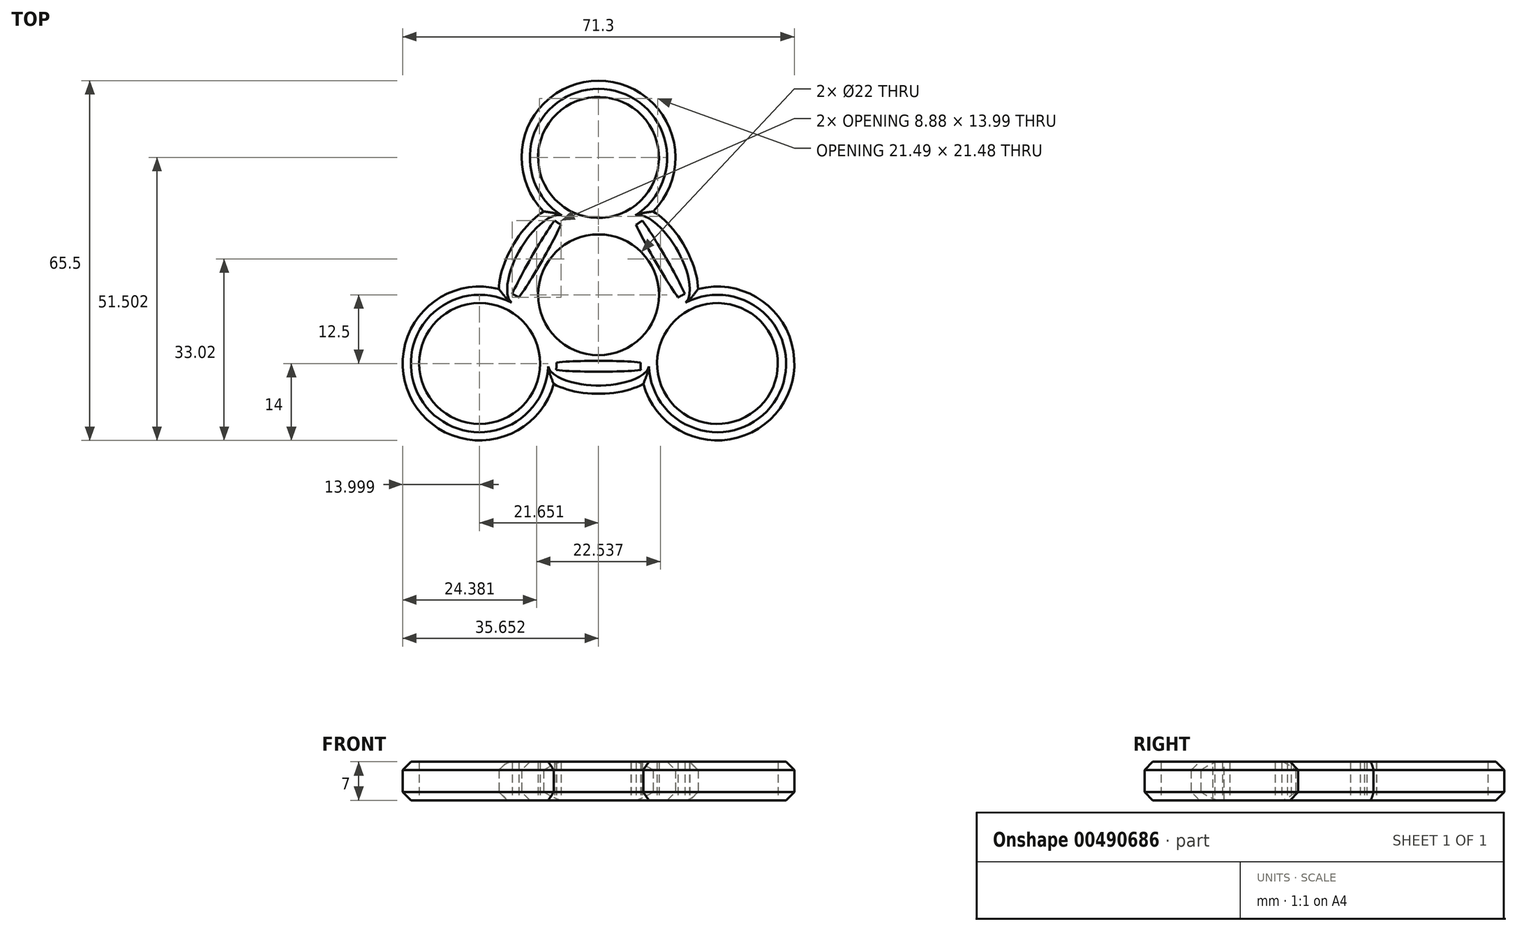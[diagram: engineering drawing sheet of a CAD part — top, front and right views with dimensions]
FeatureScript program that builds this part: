
annotation { "Feature Type Name" : "Feature", "Feature Type Description" : "" }
export const myFeature = defineFeature(function(context is Context, id is Id, definition is map)
    precondition{}
    {
        {
            var Q0;
            Q0=qCreatedBy(makeId("Top.planeOp"),FACE);
            var sketch = newSketch(context, id + "F0", { "sketchPlane" : qUnion([Q0])});
            skCircle(sketch, "E0", {"center": v(0, 0) * mm, "radius": 11 * mm});
            skCircle(sketch, "E1", {"center": v(0, 25) * mm, "radius": 11 * mm});
            skCircle(sketch, "E2.0", {"center": v(0, 25) * mm, "radius": 14 * mm});
            skCircle(sketch, "E3.1.0", {"center": v(-21.65, -12.5) * mm, "radius": 14 * mm});
            skCircle(sketch, "E3.1.1", {"center": v(-21.65, -12.5) * mm, "radius": 11 * mm});
            skCircle(sketch, "E3.2.0", {"center": v(21.65, -12.5) * mm, "radius": 14 * mm});
            skCircle(sketch, "E3.2.1", {"center": v(21.65, -12.5) * mm, "radius": 11 * mm});
            skLineSegment(sketch, "E4", {"start": v(0, 0) * mm, "end": v(9.53, 5.5) * mm});
            skLineSegment(sketch, "E5", {"start": v(9.53, 5.5) * mm, "end": v(11.26, 6.5) * mm});
            skLineSegment(sketch, "E6", {"start": v(5.9, 15.72) * mm, "end": v(0, 25) * mm});
            skLineSegment(sketch, "E7", {"start": v(11.26, 6.5) * mm, "end": v(15.59, 9) * mm});
            skEllipticalArc(sketch, "E8.trimOffspring", {});
            skEllipticalArc(sketch, "E9.trimOffspring", {});
            skPoint(sketch, "E10", {"position": v(10.4, 6) * mm});
            skEllipticalArc(sketch, "E11", {});
            skEllipticalArc(sketch, "E12.trimOffspring", {});
            skEllipticalArc(sketch, "E13.trimOffspring", {});
            skEllipticalArc(sketch, "E14.trimOffspring", {});
            skEllipticalArc(sketch, "E15.trimOffspring", {});
            skEllipticalArc(sketch, "E16.trimOffspring", {});
            skEllipticalArc(sketch, "E17.1.0", {});
            skEllipticalArc(sketch, "E17.1.1", {});
            skEllipticalArc(sketch, "E17.1.2", {});
            skEllipticalArc(sketch, "E17.2.0", {});
            skEllipticalArc(sketch, "E17.2.1", {});
            skEllipticalArc(sketch, "E17.2.2", {});
            const initialGuessF0  = {"E8.trimOffspring": [0.01125833024919717, 0.0065, 0.8660254037844385, 0.5, 0.005, 0.010660936978134876, 4.682803479661057, 4.717966405982033], "E9.trimOffspring": [0.01125833024919717, 0.0065, -0.8660254037844385, -0.5, 0.002, 0.010661807649901498, 1.556852383236011, 1.584740270353764], "E11": [0.01125833024919717, 0.0065, -0.8660254037844386, -0.5, 0.001, 0.010664918934220318, 4.684498381173167, 4.740279579596198], "E8.trimOffspring": [0.01125833024919717, 0.0065, 0.8660254037844385, 0.5, 0.005, 0.01066093697813487, 4.682803479661057, 4.7179664059820325], "E12.trimOffspring": [0.01125833024919717, 0.0065, 0.8660254037844385, 0.5, 0.005, 0.01066093697813487, 1.565218901197495, 1.6003818275303778], "E13.trimOffspring": [0.01125833024919717, 0.0065, -0.8660254037844386, -0.5, 0.001, 0.010664918934220318, 5.482987378517246, 0.8001979286625209], "E14.trimOffspring": [0.01125833024919717, 0.0065, 0.8660254037844385, 0.5, 0.005, 0.01066093697813487, 5.412354235743484, 0.8708310714359309], "E15.trimOffspring": [0.01125833024919717, 0.0065, -0.8660254037844386, -0.5, 0.001, 0.010664918934220318, 2.3347169685646114, 3.9484683386147137], "E16.trimOffspring": [0.01125833024919717, 0.0065, -0.8660254037844386, -0.5, 0.001, 0.010664918934220318, 1.5429057275836113, 1.5986869260061582], "E17.1.0": [-0.011258330249198182, 0.0065, -0.8660254037844388, 0.5, 0.005, 0.01066093697813487, 5.412354235743484, 0.8708310714359309], "E17.1.1": [-0.01125833024919818, 0.0065, 0.8660254037844388, -0.5, 0.001, 0.010664918934220318, 2.3347169685646114, 3.9484683386147137], "E17.1.2": [-0.01125833024919818, 0.0065, 0.8660254037844388, -0.5, 0.001, 0.010664918934220318, 5.482987378517246, 0.8001979286625209], "E17.2.0": [0, -0.013, 0, -1, 0.005, 0.01066093697813487, 5.412354235743484, 0.8708310714359309], "E17.2.1": [0, -0.013, 0, 1, 0.001, 0.010664918934220318, 2.3347169685646114, 3.9484683386147137], "E17.2.2": [0, -0.013, 0, 1, 0.001, 0.010664918934220318, 5.482987378517246, 0.8001979286625209]};
            skSetInitialGuess(sketch, initialGuessF0);
            skSolve(sketch);
        }
        {
            var Q0;
            {var subQ0=sQuery(id+"F0.wireOp",EDGE,"E12.trimOffspring");var subQ3=sQuery(id+"F0.wireOp",EDGE,"E1");var subQ13=makeQuery(id+"F0.imprint","INTERSECT",VERTEX,{"derivedFrom":[subQ3,subQ0]});Q0=makeQuery(id+"F0.imprint","IMPRINT",FACE,{"disambiguationData":[TD([[makeQuery(id+"F0.imprint","IMPRINT",EDGE,{"disambiguationData":[TD([[subQ13,1.0]])],"derivedFrom":subQ3}),-1.0]])]});}
            var Q1;
            {var subQ0=sQuery(id+"F0.wireOp",EDGE,"E14.trimOffspring");var subQ1=sQuery(id+"F0.wireOp",EDGE,"E2.0");var subQ2=makeQuery(id+"F0.imprint","INTERSECT",VERTEX,{"derivedFrom":[subQ1,subQ0]});Q1=makeQuery(id+"F0.imprint","IMPRINT",FACE,{"disambiguationData":[TD([[makeQuery(id+"F0.imprint","IMPRINT",EDGE,{"disambiguationData":[TD([[subQ2,1.0]])],"derivedFrom":subQ1}),-1.0]])]});}
            var Q2;
            {var subQ0=sQuery(id+"F0.wireOp",EDGE,"E14.trimOffspring");var subQ1=sQuery(id+"F0.wireOp",EDGE,"E3.2.0");var subQ2=makeQuery(id+"F0.imprint","INTERSECT",VERTEX,{"derivedFrom":[subQ1,subQ0]});Q2=makeQuery(id+"F0.imprint","IMPRINT",FACE,{"disambiguationData":[TD([[makeQuery(id+"F0.imprint","IMPRINT",EDGE,{"disambiguationData":[TD([[subQ2,-1.0]])],"derivedFrom":subQ1}),-1.0]])]});}
            var Q3;
            {var subQ0=sQuery(id+"F0.wireOp",EDGE,"E5");var subQ1=sQuery(id+"F0.wireOp",EDGE,"E0");var subQ2=makeQuery(id+"F0.imprint","INTERSECT",VERTEX,{"derivedFrom":[subQ1,subQ0]});Q3=makeQuery(id+"F0.imprint","IMPRINT",FACE,{"disambiguationData":[TD([[makeQuery(id+"F0.imprint","IMPRINT",EDGE,{"disambiguationData":[TD([[subQ2,-1.0]])],"derivedFrom":subQ1}),-1.0]])]});}
            var Q4;
            {var subQ0=sQuery(id+"F0.wireOp",EDGE,"E5");var subQ1=sQuery(id+"F0.wireOp",EDGE,"E0");var subQ2=makeQuery(id+"F0.imprint","INTERSECT",VERTEX,{"derivedFrom":[subQ1,subQ0]});Q4=makeQuery(id+"F0.imprint","IMPRINT",FACE,{"disambiguationData":[TD([[makeQuery(id+"F0.imprint","IMPRINT",EDGE,{"disambiguationData":[TD([[subQ2,1.0]])],"derivedFrom":subQ1}),-1.0]])]});}
            var Q5;
            {var subQ5=sQuery(id+"F0.wireOp",EDGE,"E17.1.2");Q5=makeQuery(id+"F0.imprint","IMPRINT",FACE,{"disambiguationData":[TD([[makeQuery(id+"F0.imprint","IMPRINT",EDGE,{"derivedFrom":subQ5}),-1.0]])]});}
            var Q6;
            {var subQ0=sQuery(id+"F0.wireOp",EDGE,"E17.1.0");Q6=makeQuery(id+"F0.imprint","IMPRINT",FACE,{"disambiguationData":[TD([[makeQuery(id+"F0.imprint","IMPRINT",EDGE,{"derivedFrom":subQ0}),1.0]])]});}
            var Q7;
            Q7=makeQuery(id+"F0.imprint","IMPRINT",FACE,{"disambiguationData":[TD([[makeQuery(id+"F0.imprint","IMPRINT",EDGE,{"derivedFrom":sQuery(id+"F0.wireOp",EDGE,"E3.1.1")}),-1.0]])]});
            var Q8;
            {var subQ5=sQuery(id+"F0.wireOp",EDGE,"E17.2.2");Q8=makeQuery(id+"F0.imprint","IMPRINT",FACE,{"disambiguationData":[TD([[makeQuery(id+"F0.imprint","IMPRINT",EDGE,{"derivedFrom":subQ5}),-1.0]])]});}
            var Q9;
            {var subQ0=sQuery(id+"F0.wireOp",EDGE,"E17.2.0");Q9=makeQuery(id+"F0.imprint","IMPRINT",FACE,{"disambiguationData":[TD([[makeQuery(id+"F0.imprint","IMPRINT",EDGE,{"derivedFrom":subQ0}),1.0]])]});}
            var Q10;
            {var subQ7=sQuery(id+"F0.wireOp",EDGE,"E3.2.0");var subQ8=makeQuery(id+"F0.imprint","INTERSECT",VERTEX,{"derivedFrom":[subQ7,sQuery(id+"F0.wireOp",EDGE,"E14.trimOffspring")]});Q10=makeQuery(id+"F0.imprint","IMPRINT",FACE,{"disambiguationData":[TD([[makeQuery(id+"F0.imprint","IMPRINT",EDGE,{"disambiguationData":[TD([[subQ8,-1.0]])],"derivedFrom":subQ7}),1.0]])]});}
            extrude(context, id + "F1", {"entities" : qUnion([Q0, Q1, Q2, Q3, Q4, Q5, Q6, Q7, Q8, Q9, Q10]), "depth" : 7 * mm});
        }
        {
            var Q0;
            {var subQ0=sQuery(id+"F0.wireOp",EDGE,"E2.0");Q0=makeQuery(id+"F1.opExtrude","CAP_EDGE",EDGE,{"disambiguationData":[OSD([subQ0]),TDD([makeQuery(id+"F0.imprint","IMPRINT",EDGE,{"disambiguationData":[TD([[makeQuery(id+"F0.imprint","INTERSECT",VERTEX,{"derivedFrom":[subQ0,sQuery(id+"F0.wireOp",EDGE,"E14.trimOffspring")]}),-1.0]])],"derivedFrom":subQ0})])],"isStart":false});}
            var Q1;
            Q1=makeQuery(id+"F1.opExtrude","CAP_EDGE",EDGE,{"disambiguationData":[OSD([sQuery(id+"F0.wireOp",EDGE,"E17.1.0")])],"isStart":false});
            var Q2;
            {var subQ0=sQuery(id+"F0.wireOp",EDGE,"E3.1.0");Q2=makeQuery(id+"F1.opExtrude","CAP_EDGE",EDGE,{"disambiguationData":[OSD([subQ0]),TDD([makeQuery(id+"F0.imprint","IMPRINT",EDGE,{"disambiguationData":[TD([[makeQuery(id+"F0.imprint","INTERSECT",VERTEX,{"derivedFrom":[subQ0,sQuery(id+"F0.wireOp",EDGE,"E17.1.0")]}),-1.0]])],"derivedFrom":subQ0})])],"isStart":false});}
            var Q3;
            Q3=makeQuery(id+"F1.opExtrude","CAP_EDGE",EDGE,{"disambiguationData":[OSD([sQuery(id+"F0.wireOp",EDGE,"E17.2.0")])],"isStart":false});
            var Q4;
            {var subQ0=sQuery(id+"F0.wireOp",EDGE,"E3.2.0");Q4=makeQuery(id+"F1.opExtrude","CAP_EDGE",EDGE,{"disambiguationData":[OSD([subQ0]),TDD([makeQuery(id+"F0.imprint","IMPRINT",EDGE,{"disambiguationData":[TD([[makeQuery(id+"F0.imprint","INTERSECT",VERTEX,{"derivedFrom":[subQ0,sQuery(id+"F0.wireOp",EDGE,"E14.trimOffspring")]}),1.0]])],"derivedFrom":subQ0})])],"isStart":false});}
            var Q5;
            Q5=makeQuery(id+"F1.opExtrude","CAP_EDGE",EDGE,{"disambiguationData":[OSD([sQuery(id+"F0.wireOp",EDGE,"E14.trimOffspring")])],"isStart":false});
            var Q6;
            {var subQ0=sQuery(id+"F0.wireOp",EDGE,"E3.2.0");Q6=makeQuery(id+"F1.opExtrude","CAP_EDGE",EDGE,{"disambiguationData":[OSD([subQ0]),TDD([makeQuery(id+"F0.imprint","IMPRINT",EDGE,{"disambiguationData":[TD([[makeQuery(id+"F0.imprint","INTERSECT",VERTEX,{"derivedFrom":[subQ0,sQuery(id+"F0.wireOp",EDGE,"E14.trimOffspring")]}),1.0]])],"derivedFrom":subQ0})])],"isStart":false});}
            var Q7;
            {var subQ0=sQuery(id+"F0.wireOp",EDGE,"E3.1.0");Q7=makeQuery(id+"F1.opExtrude","CAP_EDGE",EDGE,{"disambiguationData":[OSD([subQ0]),TDD([makeQuery(id+"F0.imprint","IMPRINT",EDGE,{"disambiguationData":[TD([[makeQuery(id+"F0.imprint","INTERSECT",VERTEX,{"derivedFrom":[subQ0,sQuery(id+"F0.wireOp",EDGE,"E17.1.0")]}),-1.0]])],"derivedFrom":subQ0})])],"isStart":true});}
            var Q8;
            Q8=makeQuery(id+"F1.opExtrude","CAP_EDGE",EDGE,{"disambiguationData":[OSD([sQuery(id+"F0.wireOp",EDGE,"E17.2.0")])],"isStart":true});
            var Q9;
            {var subQ0=sQuery(id+"F0.wireOp",EDGE,"E3.2.0");Q9=makeQuery(id+"F1.opExtrude","CAP_EDGE",EDGE,{"disambiguationData":[OSD([subQ0]),TDD([makeQuery(id+"F0.imprint","IMPRINT",EDGE,{"disambiguationData":[TD([[makeQuery(id+"F0.imprint","INTERSECT",VERTEX,{"derivedFrom":[subQ0,sQuery(id+"F0.wireOp",EDGE,"E14.trimOffspring")]}),1.0]])],"derivedFrom":subQ0})])],"isStart":true});}
            var Q10;
            Q10=makeQuery(id+"F1.opExtrude","CAP_EDGE",EDGE,{"disambiguationData":[OSD([sQuery(id+"F0.wireOp",EDGE,"E14.trimOffspring")])],"isStart":true});
            var Q11;
            {var subQ0=sQuery(id+"F0.wireOp",EDGE,"E2.0");Q11=makeQuery(id+"F1.opExtrude","CAP_EDGE",EDGE,{"disambiguationData":[OSD([subQ0]),TDD([makeQuery(id+"F0.imprint","IMPRINT",EDGE,{"disambiguationData":[TD([[makeQuery(id+"F0.imprint","INTERSECT",VERTEX,{"derivedFrom":[subQ0,sQuery(id+"F0.wireOp",EDGE,"E14.trimOffspring")]}),-1.0]])],"derivedFrom":subQ0})])],"isStart":true});}
            var Q12;
            Q12=makeQuery(id+"F1.opExtrude","CAP_EDGE",EDGE,{"disambiguationData":[OSD([sQuery(id+"F0.wireOp",EDGE,"E17.1.0")])],"isStart":true});
            chamfer(context, id + "F2", {"entities" : qUnion([Q0, Q1, Q2, Q3, Q4, Q5, Q6, Q7, Q8, Q9, Q10, Q11, Q12]), "width" : 1.5 * mm, "tangentPropagation" : true});
        }
    });
